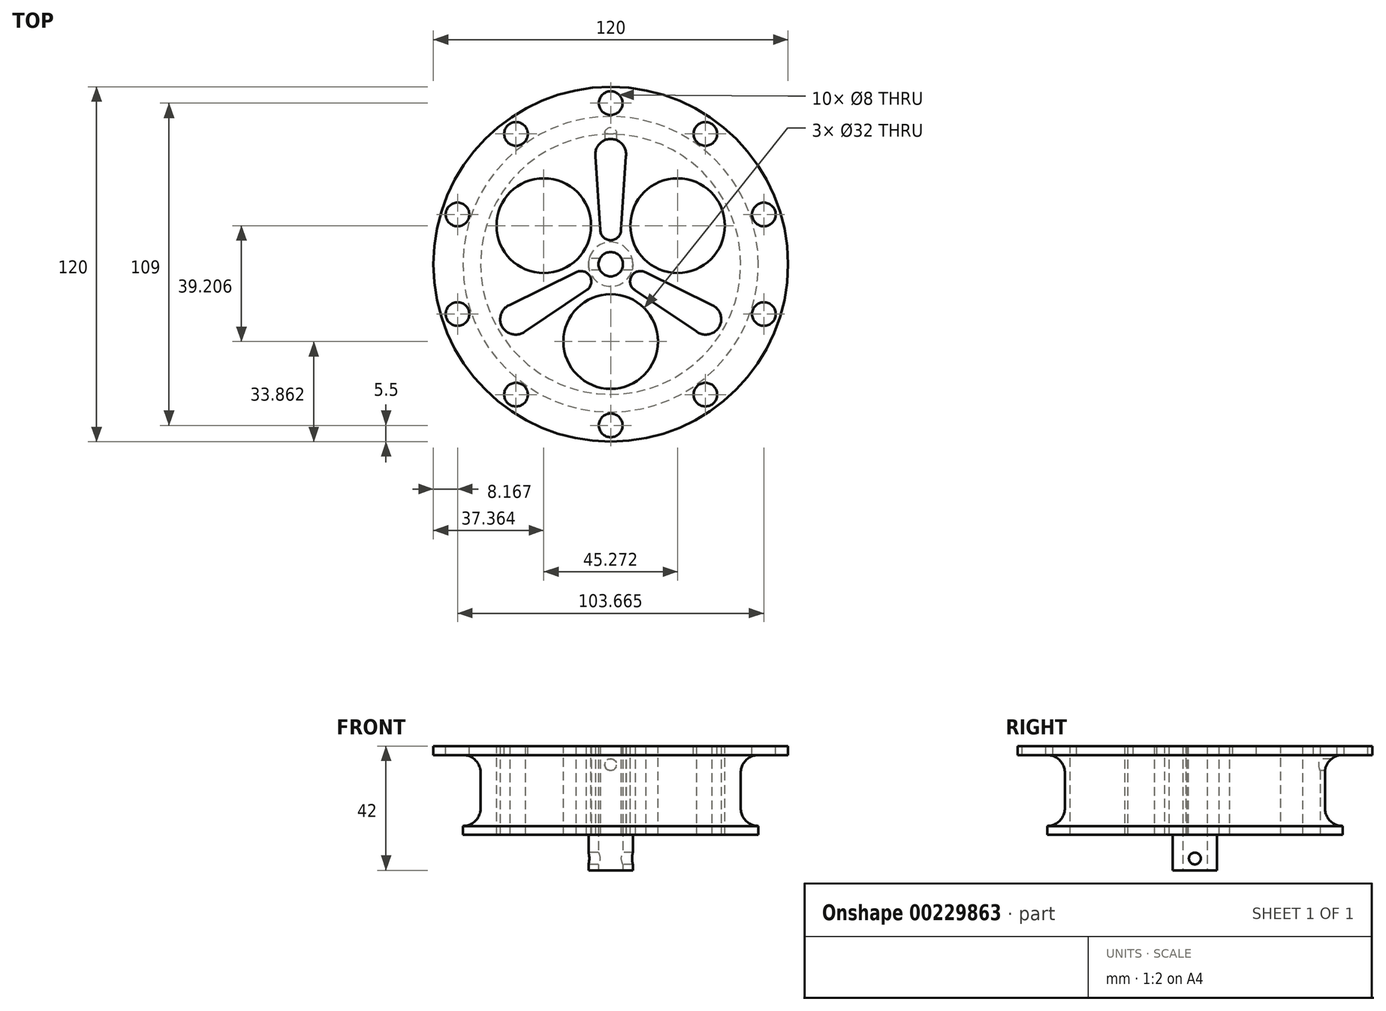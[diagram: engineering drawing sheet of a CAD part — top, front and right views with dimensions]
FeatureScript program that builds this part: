
annotation { "Feature Type Name" : "Feature", "Feature Type Description" : "" }
export const myFeature = defineFeature(function(context is Context, id is Id, definition is map)
    precondition{}
    {
        {
            var Q0;
            Q0=qCreatedBy(makeId("Top.planeOp"),FACE);
            var sketch = newSketch(context, id + "F0", { "sketchPlane" : qUnion([Q0])});
            skCircle(sketch, "E0", {"center": v(0, 0) * mm, "radius": 4.12 * mm});
            skCircle(sketch, "E1", {"center": v(0, 0) * mm, "radius": 7.5 * mm});
            skCircle(sketch, "E2", {"center": v(0, 0) * mm, "radius": 50 * mm});
            skLineSegment(sketch, "E3", {"start": v(0, 0) * mm, "end": v(0, 50) * mm, "construction": true});
            skCircle(sketch, "E4", {"center": v(0, 37.15) * mm, "radius": 5.22 * mm});
            skCircle(sketch, "E5", {"center": v(0, 11.6) * mm, "radius": 3.5 * mm});
            skPoint(sketch, "E6", {"position": v(-5.22, 37.15) * mm});
            skPoint(sketch, "E7", {"position": v(5.22, 37.15) * mm});
            skPoint(sketch, "E8", {"position": v(3.5, 11.6) * mm});
            skPoint(sketch, "E9", {"position": v(-3.5, 11.6) * mm});
            skLineSegment(sketch, "E10", {"start": v(-5.22, 37.15) * mm, "end": v(-3.5, 11.6) * mm});
            skLineSegment(sketch, "E11", {"start": v(5.22, 37.15) * mm, "end": v(3.5, 11.6) * mm});
            skCircle(sketch, "E12.1.0", {"center": v(-32.17, -18.57) * mm, "radius": 5.22 * mm});
            skLineSegment(sketch, "E12.1.1", {"start": v(-34.78, -14.05) * mm, "end": v(-11.8, -2.77) * mm});
            skCircle(sketch, "E12.1.2", {"center": v(-10.05, -5.8) * mm, "radius": 3.5 * mm});
            skLineSegment(sketch, "E12.1.3", {"start": v(-29.56, -23.1) * mm, "end": v(-8.3, -8.84) * mm});
            skCircle(sketch, "E12.2.0", {"center": v(32.17, -18.57) * mm, "radius": 5.22 * mm});
            skLineSegment(sketch, "E12.2.1", {"start": v(29.56, -23.1) * mm, "end": v(8.3, -8.84) * mm});
            skCircle(sketch, "E12.2.2", {"center": v(10.05, -5.8) * mm, "radius": 3.5 * mm});
            skLineSegment(sketch, "E12.2.3", {"start": v(34.78, -14.05) * mm, "end": v(11.8, -2.77) * mm});
            skSolve(sketch);
        }
        {
            var Q0;
            Q0=makeQuery(id+"F0.imprint","IMPRINT",FACE,{"disambiguationData":[TD([[makeQuery(id+"F0.imprint","IMPRINT",EDGE,{"derivedFrom":sQuery(id+"F0.wireOp",EDGE,"E1")}),-1.0]])]});
            var Q1;
            Q1=makeQuery(id+"F0.imprint","IMPRINT",FACE,{"disambiguationData":[TD([[makeQuery(id+"F0.imprint","IMPRINT",EDGE,{"derivedFrom":sQuery(id+"F0.wireOp",EDGE,"E0")}),-1.0]])]});
            extrude(context, id + "F1", {"entities" : qUnion([Q0, Q1]), "depth" : 30 * mm});
        }
        {
            var Q0;
            Q0=qCreatedBy(makeId("Front.planeOp"),FACE);
            var sketch = newSketch(context, id + "F2", { "sketchPlane" : qUnion([Q0])});
            skLineSegment(sketch, "E13.0", {"start": v(-50, 30) * mm, "end": v(50, 30) * mm});
            skLineSegment(sketch, "E14.0", {"start": v(-50, 0) * mm, "end": v(50, 0) * mm});
            skCircle(sketch, "E15", {"center": v(0, 16.12) * mm, "radius": 1.86 * mm});
            skSolve(sketch);
        }
        {
            var Q0;
            Q0=makeQuery(id+"F0.imprint","IMPRINT",FACE,{"disambiguationData":[TD([[makeQuery(id+"F0.imprint","IMPRINT",EDGE,{"derivedFrom":sQuery(id+"F0.wireOp",EDGE,"E0")}),-1.0]])]});
            extrude(context, id + "F3", {"entities" : qUnion([Q0]), "operationType" : NewBodyOperationType.ADD, "oppositeDirection" : true, "depth" : 12 * mm});
        }
        {
            var Q0;
            Q0=qCreatedBy(makeId("Right.planeOp"),FACE);
            var sketch = newSketch(context, id + "F4", { "sketchPlane" : qUnion([Q0])});
            skLineSegment(sketch, "E16.0", {"start": v(-7.5, -12) * mm, "end": v(7.5, -12) * mm});
            skPoint(sketch, "E17", {"position": v(0, -10) * mm});
            skPoint(sketch, "E17.positionSnap0", {"position": v(0, -12) * mm});
            skPoint(sketch, "E18", {"position": v(0, -8) * mm});
            skCircle(sketch, "E19", {"center": v(0, -8) * mm, "radius": 2 * mm});
            skSolve(sketch);
        }
        {
            var Q0;
            Q0=makeQuery(id+"F4.imprint","IMPRINT",FACE,{"disambiguationData":[TD([[makeQuery(id+"F4.imprint","IMPRINT",EDGE,{"derivedFrom":sQuery(id+"F4.wireOp",EDGE,"E19")}),1.0]])]});
            extrude(context, id + "F5", {"entities" : qUnion([Q0]), "operationType" : NewBodyOperationType.REMOVE, "depth" : 25 * mm, "hasSecondDirection" : true, "secondDirectionOppositeDirection" : true, "secondDirectionDepth" : 25 * mm});
        }
        {
            var Q0;
            Q0=qCreatedBy(makeId("Right.planeOp"),FACE);
            var sketch = newSketch(context, id + "F6", { "sketchPlane" : qUnion([Q0])});
            skLineSegment(sketch, "E20.0", {"start": v(-50, 30) * mm, "end": v(50, 30) * mm});
            skLineSegment(sketch, "E21.0", {"start": v(-50, 0) * mm, "end": v(50, 0) * mm});
            skLineSegment(sketch, "E22", {"start": v(50, 0) * mm, "end": v(50, 3) * mm});
            skLineSegment(sketch, "E23", {"start": v(50, 3) * mm, "end": v(50, 3) * mm});
            skLineSegment(sketch, "E24", {"start": v(44, 9) * mm, "end": v(44, 21) * mm});
            skLineSegment(sketch, "E25", {"start": v(50, 27) * mm, "end": v(50, 27) * mm});
            skLineSegment(sketch, "E26", {"start": v(50, 27) * mm, "end": v(50, 30) * mm});
            skLineSegment(sketch, "E27", {"start": v(50, 27) * mm, "end": v(53.94, 27) * mm});
            skLineSegment(sketch, "E28", {"start": v(53.94, 27) * mm, "end": v(53.94, 3) * mm});
            skLineSegment(sketch, "E29", {"start": v(53.94, 3) * mm, "end": v(50, 3) * mm});
            skLineSegment(sketch, "E30", {"start": v(0, 0) * mm, "end": v(0, 34.05) * mm});
            skPoint(sketch, "E31.visualSharp", {"position": v(44, 27) * mm});
            skArc(sketch, "E31.filletArc", {"start": v(50, 27) * mm, "mid": v(45.76, 25.24) * mm, "end": v(44, 21) * mm});
            skPoint(sketch, "E32.visualSharp", {"position": v(44, 3) * mm});
            skArc(sketch, "E32.filletArc", {"start": v(44, 9) * mm, "mid": v(45.76, 4.76) * mm, "end": v(50, 3) * mm});
            skSolve(sketch);
        }
        {
            var Q0;
            Q0=makeQuery(id+"F6.imprint","IMPRINT",FACE,{"disambiguationData":[TD([[makeQuery(id+"F6.imprint","IMPRINT",EDGE,{"derivedFrom":sQuery(id+"F6.wireOp",EDGE,"E24")}),-1.0]])]});
            var Q1;
            Q1=sQuery(id+"F6.wireOp",EDGE,"E30");
            revolve(context, id + "F7", {"operationType" : NewBodyOperationType.REMOVE, "entities" : qUnion([Q0]), "axis" : qUnion([Q1]), "revolveType" : RevolveType.FULL, "oppositeDirection" : true});
        }
        {
            var Q0;
            Q0=makeQuery(id+"F1.opExtrude","CAP_FACE",FACE,{"disambiguationData":[OSD([sQuery(id+"F0.wireOp",EDGE,"E0"),sQuery(id+"F0.wireOp",EDGE,"E2"),sQuery(id+"F0.wireOp",EDGE,"E4"),sQuery(id+"F0.wireOp",EDGE,"E5"),sQuery(id+"F0.wireOp",EDGE,"E10"),sQuery(id+"F0.wireOp",EDGE,"E11"),sQuery(id+"F0.wireOp",EDGE,"E12.1.0"),sQuery(id+"F0.wireOp",EDGE,"E12.1.1"),sQuery(id+"F0.wireOp",EDGE,"E12.1.2"),sQuery(id+"F0.wireOp",EDGE,"E12.1.3"),sQuery(id+"F0.wireOp",EDGE,"E12.2.0"),sQuery(id+"F0.wireOp",EDGE,"E12.2.1"),sQuery(id+"F0.wireOp",EDGE,"E12.2.2"),sQuery(id+"F0.wireOp",EDGE,"E12.2.3")])],"isStart":false});
            var sketch = newSketch(context, id + "F8", { "sketchPlane" : qUnion([Q0])});
            skPoint(sketch, "E33", {"position": v(0, -26.14) * mm});
            skCircle(sketch, "E34", {"center": v(0, -26.14) * mm, "radius": 16 * mm});
            skCircle(sketch, "E35.1.0", {"center": v(22.64, 13.07) * mm, "radius": 16 * mm});
            skCircle(sketch, "E35.2.0", {"center": v(-22.64, 13.07) * mm, "radius": 16 * mm});
            skPoint(sketch, "E35.center", {"position": v(0, 0) * mm});
            skSolve(sketch);
        }
        {
            var Q0;
            Q0=makeQuery(id+"F8.imprint","IMPRINT",FACE,{"disambiguationData":[TD([[makeQuery(id+"F8.imprint","IMPRINT",EDGE,{"derivedFrom":sQuery(id+"F8.wireOp",EDGE,"E35.2.0")}),1.0]])]});
            var Q1;
            Q1=makeQuery(id+"F8.imprint","IMPRINT",FACE,{"disambiguationData":[TD([[makeQuery(id+"F8.imprint","IMPRINT",EDGE,{"derivedFrom":sQuery(id+"F8.wireOp",EDGE,"E35.1.0")}),1.0]])]});
            var Q2;
            Q2=makeQuery(id+"F8.imprint","IMPRINT",FACE,{"disambiguationData":[TD([[makeQuery(id+"F8.imprint","IMPRINT",EDGE,{"derivedFrom":sQuery(id+"F8.wireOp",EDGE,"E34")}),1.0]])]});
            extrude(context, id + "F9", {"entities" : qUnion([Q0, Q1, Q2]), "operationType" : NewBodyOperationType.REMOVE, "oppositeDirection" : true, "depth" : 44.4 * mm});
        }
        {
            var Q0;
            Q0=makeQuery(id+"F1.opExtrude","CAP_FACE",FACE,{"disambiguationData":[OSD([sQuery(id+"F0.wireOp",EDGE,"E0"),sQuery(id+"F0.wireOp",EDGE,"E2"),sQuery(id+"F0.wireOp",EDGE,"E4"),sQuery(id+"F0.wireOp",EDGE,"E5"),sQuery(id+"F0.wireOp",EDGE,"E10"),sQuery(id+"F0.wireOp",EDGE,"E11"),sQuery(id+"F0.wireOp",EDGE,"E12.1.0"),sQuery(id+"F0.wireOp",EDGE,"E12.1.1"),sQuery(id+"F0.wireOp",EDGE,"E12.1.2"),sQuery(id+"F0.wireOp",EDGE,"E12.1.3"),sQuery(id+"F0.wireOp",EDGE,"E12.2.0"),sQuery(id+"F0.wireOp",EDGE,"E12.2.1"),sQuery(id+"F0.wireOp",EDGE,"E12.2.2"),sQuery(id+"F0.wireOp",EDGE,"E12.2.3")])],"isStart":false});
            var sketch = newSketch(context, id + "F10", { "sketchPlane" : qUnion([Q0])});
            skCircle(sketch, "E36.0", {"center": v(0, 0) * mm, "radius": 50 * mm});
            skCircle(sketch, "E37", {"center": v(0, 0) * mm, "radius": 60 * mm});
            skPoint(sketch, "E38", {"position": v(0, 54.5) * mm});
            skPoint(sketch, "E38.positionSnap0", {"position": v(0, 42.37) * mm});
            skCircle(sketch, "E39", {"center": v(0, 54.5) * mm, "radius": 4 * mm});
            skCircle(sketch, "E40.1.0", {"center": v(-32.03, 44.1) * mm, "radius": 4 * mm});
            skCircle(sketch, "E40.2.0", {"center": v(-51.83, 16.84) * mm, "radius": 4 * mm});
            skCircle(sketch, "E40.3.0", {"center": v(-51.83, -16.84) * mm, "radius": 4 * mm});
            skCircle(sketch, "E40.4.0", {"center": v(-32.03, -44.1) * mm, "radius": 4 * mm});
            skCircle(sketch, "E40.5.0", {"center": v(0, -54.5) * mm, "radius": 4 * mm});
            skCircle(sketch, "E40.6.0", {"center": v(32.03, -44.1) * mm, "radius": 4 * mm});
            skCircle(sketch, "E40.7.0", {"center": v(51.83, -16.84) * mm, "radius": 4 * mm});
            skCircle(sketch, "E40.8.0", {"center": v(51.83, 16.84) * mm, "radius": 4 * mm});
            skCircle(sketch, "E40.9.0", {"center": v(32.03, 44.1) * mm, "radius": 4 * mm});
            skSolve(sketch);
        }
        {
            var Q0;
            Q0=makeQuery(id+"F10.imprint","IMPRINT",FACE,{"disambiguationData":[TD([[makeQuery(id+"F10.imprint","IMPRINT",EDGE,{"derivedFrom":sQuery(id+"F10.wireOp",EDGE,"E36.0")}),-1.0]])]});
            extrude(context, id + "F11", {"entities" : qUnion([Q0]), "operationType" : NewBodyOperationType.ADD, "oppositeDirection" : true, "depth" : 3 * mm});
        }
        {
            var Q0;
            Q0=qCreatedBy(makeId("Front.planeOp"),FACE);
            var sketch = newSketch(context, id + "F12", { "sketchPlane" : qUnion([Q0])});
            skLineSegment(sketch, "E41.0", {"start": v(-50, 30) * mm, "end": v(50, 30) * mm});
            skLineSegment(sketch, "E41.1", {"start": v(-60, 27) * mm, "end": v(60, 27) * mm});
            skPoint(sketch, "E42", {"position": v(0, 23.73) * mm});
            skPoint(sketch, "E42.positionSnap0", {"position": v(0, 27) * mm});
            skCircle(sketch, "E43", {"center": v(0, 23.73) * mm, "radius": 2 * mm});
            skSolve(sketch);
        }
        {
            var Q0;
            Q0=makeQuery(id+"F12.imprint","IMPRINT",FACE,{"disambiguationData":[TD([[makeQuery(id+"F12.imprint","IMPRINT",EDGE,{"derivedFrom":sQuery(id+"F12.wireOp",EDGE,"E43")}),1.0]])]});
            extrude(context, id + "F13", {"entities" : qUnion([Q0]), "operationType" : NewBodyOperationType.REMOVE, "oppositeDirection" : true, "depth" : 94.6 * mm, "hasSecondDirection" : true, "secondDirectionOppositeDirection" : true, "secondDirectionDepth" : 18.6 * mm});
        }
    });
